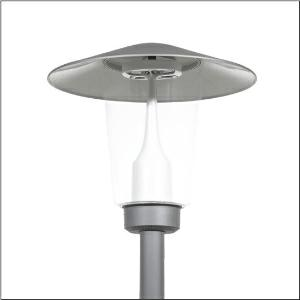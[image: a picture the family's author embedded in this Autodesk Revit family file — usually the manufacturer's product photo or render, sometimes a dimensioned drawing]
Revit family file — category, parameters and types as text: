
# Revit family: pilzleuchte_iq___st1_2a_5xa5235af14hp_844e
name_source: partatom
category: Lighting Fixtures
units: mm (PartAtom-declared; Revit-internal decimal feet)

## family parameters
Cut with Voids When Loaded = No
Host = Face
Light Source = No
Part Type = Normal
Room Calculation Point = No
Round Connector Dimension = Use Diameter
Shared = No

## types (1)
- --- (1 x LED, 3950 lm, 33.6 W, 2200K)
    Apparent Load = 34 VA
    CIE Flux Codes = 23 60 92 98 100
    Color Rendering = 70
    Color Temperature = 2200K
    Default Elevation = 1800 mm
    Description = Mushroom Luminaire iQ, mast luminaire, Module 540 iQ-SR, primary light control with 3 zone facetted reflector, of plastic, silver coated, highly specular, structured, primary optical cover: cover, of PMMA, transparent, light distribution: ST1.2a, light emission: direct distribution, primary light characteristic: asymmetric, installation type: post-top, LED, High Power LED, rated luminous flux: 3.950lm, luminous efficacy: 117lm/W, light colour: 722, colour temperature: 2200K, control gear: ECG iQ, control: pre-setting: logarithmic dimming characteristic, Street-Remote, Auto-Match, Temp-Guard, Lumen-Switch, Night-Set, Smart-Wire, Light-Fading, Desk-Remote (wireless, voltage-free reading and setting of iQ features in the workshop via application-optimized NFC function/RFID function), optimised constant luminous flux control (CLO 2.0), with terminal, 6-pole, max. 2.5mm², mains connection: 230..240V, AC, 50/60Hz, start of lifetime: 34W, end of service life: 36W, reduction: 15W, luminaire housing, upper part, of glass-fibre reinforced polyester, coated, Siteco® metallic grey (DB 702S), diameter: 650mm, height: 586mm, spigot size: d x l = 76 x 70mm (post-top) | with reducer (optional accessory) 60 x 70mm, post-top mast mounting element, of diecast aluminium, coated, Siteco® metallic grey (DB 702S), Module 540 iQ-SR, traffic white (RAL 9016), equipment: Power, protection rating (complete): IP65, insulation class (complete): insulation class II (safety insulation), certification: CE, ENEC, VDE, packaging unit: 1 piece

Light Distribution: ST1.2a
    Height = 586 mm
    Lamp = 1 x LED
    Lamp Light Flux = 3950 lm
    Lamp Power = 33.6 W
    Lamp count = 1
    Length = 650 mm
    Luminous efficacy = 118 lm/W
    Manufacturer = Siteco
    ModVariant = No
    Model = 5XA5235AF14HP
    Number of Poles = 1
    OnlyDefault = Yes
    Power Factor = 1
    Product Name = Pilzleuchte iQ | ST1.2a
    Product group = mast luminaire | pylon top
    ProductGroupID = 6100
    Protection Class = Protection class II
    Protection Degree = IP 65
    RLX_Detail_Level = 1
    RLX_Emergency_Light_Flux = 0 lm
    RLX_Emergency_Type = 0
    RLX_Emergency_Type_DB = No
    RlxData = <blob elided: 51509 chars, md5=ad0db857>
    Socket = socket
    Standby Power = 0 W
    System Light Flux = 3950 lm
    System Power = 34 W
    Type Comments = factory setting: luminous flux: 100 % | dim-lin: 254 | 695 mA
    Type Image = l_1006077.jpg
    URL = http://relux.com
    VarID = @adj_166343
    Voltage = 0 V
    Weight = 0.00 kg
    Width = 0 mm  [stored 0 ft]

note: [stored X ft] marks values corroborated as IEEE doubles in the binary element streams (Revit-internal decimal feet)

## geometry (parser evidence)
native form markers: Blend x4, Sweep x12
no freeform markers — native parametric forms only
